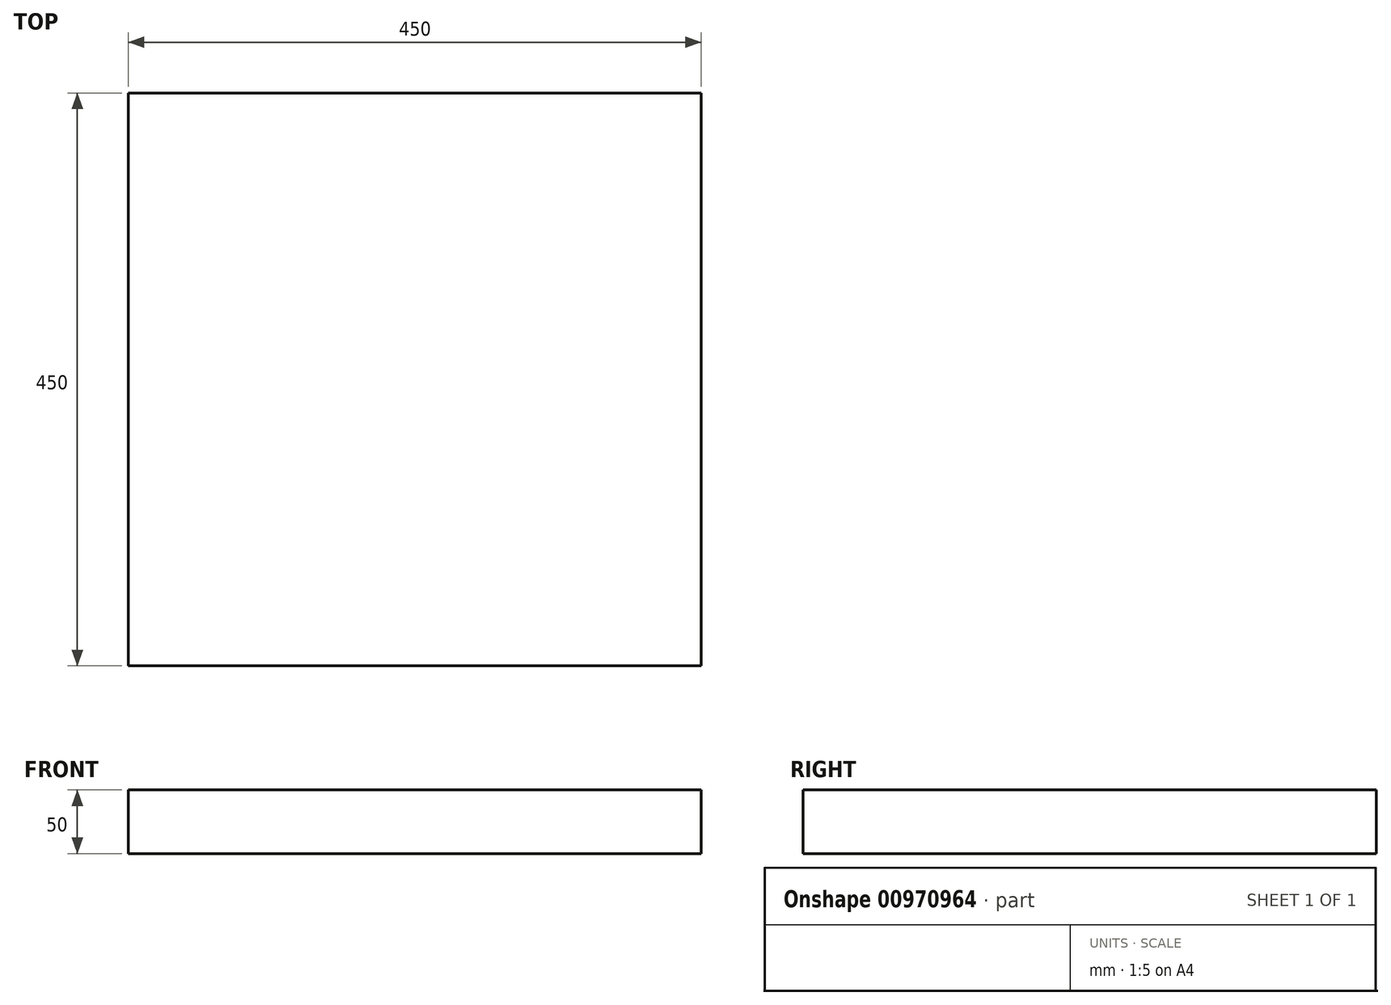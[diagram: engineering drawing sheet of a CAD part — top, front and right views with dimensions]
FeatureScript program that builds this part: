
annotation { "Feature Type Name" : "Feature", "Feature Type Description" : "" }
export const myFeature = defineFeature(function(context is Context, id is Id, definition is map)
    precondition{}
    {
        {
            var Q0;
            Q0=qCreatedBy(makeId("Top.planeOp"),FACE);
            var sketch = newSketch(context, id + "F0", { "sketchPlane" : qUnion([Q0])});
            skLineSegment(sketch, "E0.bottom", {"start": v(225, 225) * mm, "end": v(-225, 225) * mm});
            skLineSegment(sketch, "E0.top", {"start": v(225, -225) * mm, "end": v(-225, -225) * mm});
            skLineSegment(sketch, "E0.left", {"start": v(225, 225) * mm, "end": v(225, -225) * mm});
            skLineSegment(sketch, "E0.right", {"start": v(-225, 225) * mm, "end": v(-225, -225) * mm});
            skPoint(sketch, "E0.middle", {"position": v(0, 0) * mm});
            skSolve(sketch);
        }
        {
            var Q0;
            Q0=makeQuery(id+"F0.imprint","IMPRINT",FACE,{"disambiguationData":[TD([[makeQuery(id+"F0.imprint","IMPRINT",EDGE,{"derivedFrom":sQuery(id+"F0.wireOp",EDGE,"E0.bottom")}),1.0]])]});
            extrude(context, id + "F1", {"entities" : qUnion([Q0]), "depth" : 50 * mm, "offsetDistance" : 25 * mm});
        }
    });
